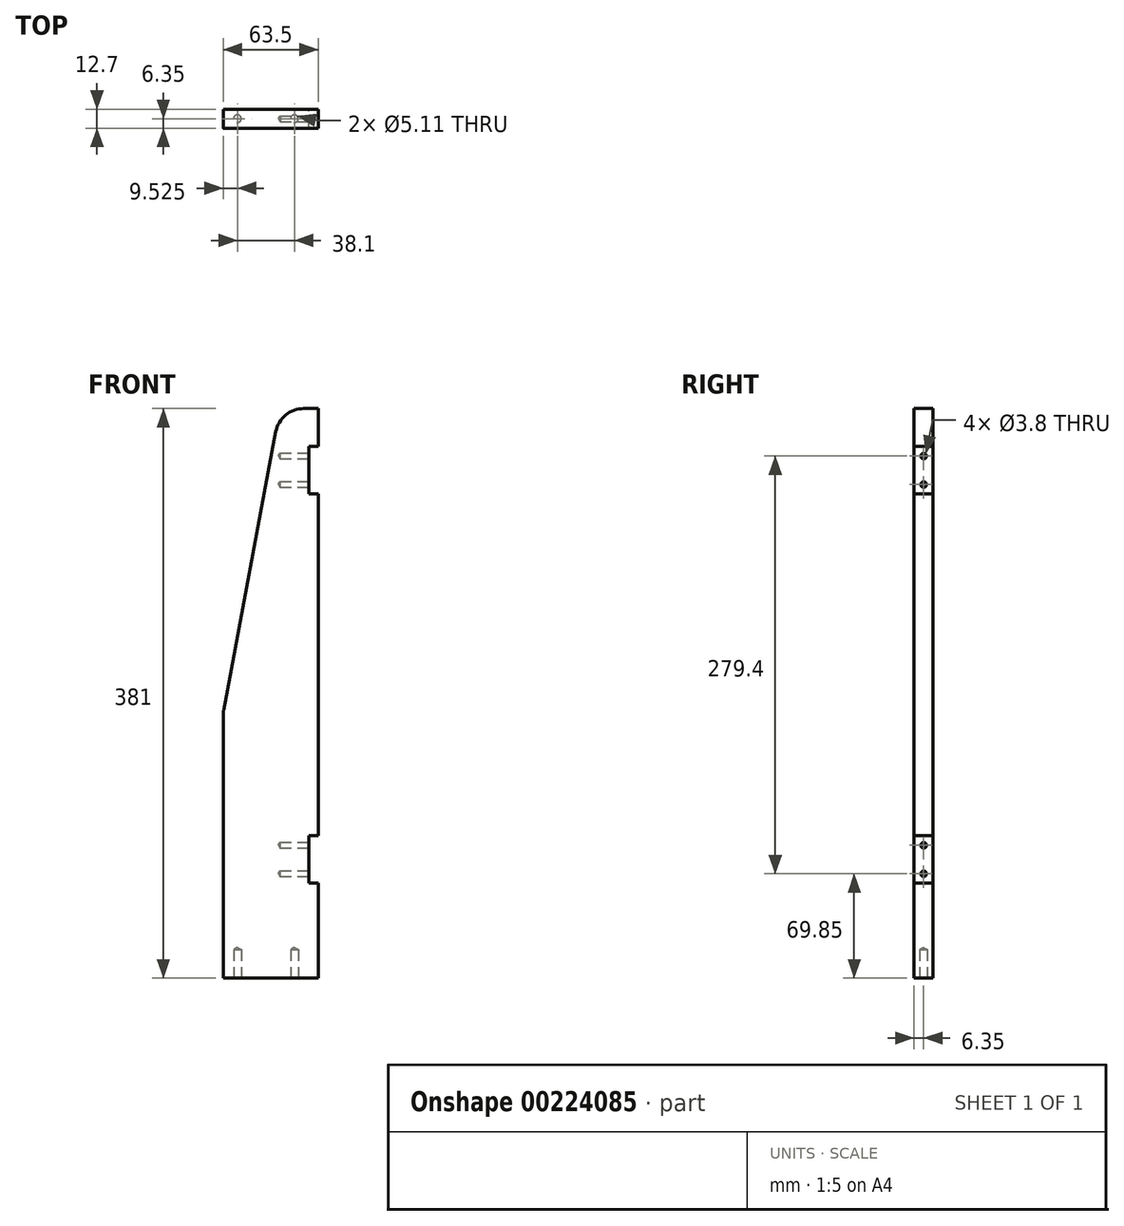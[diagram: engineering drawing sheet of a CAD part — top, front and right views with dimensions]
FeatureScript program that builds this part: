
annotation { "Feature Type Name" : "Feature", "Feature Type Description" : "" }
export const myFeature = defineFeature(function(context is Context, id is Id, definition is map)
    precondition{}
    {
        {
            var Q0;
            Q0=qCreatedBy(makeId("Top.planeOp"),FACE);
            var sketch = newSketch(context, id + "F0", { "sketchPlane" : qUnion([Q0])});
            skLineSegment(sketch, "E0.bottom", {"start": v(0, 0) * mm, "end": v(-63.5, 0) * mm});
            skLineSegment(sketch, "E0.top", {"start": v(0, 12.7) * mm, "end": v(-63.5, 12.7) * mm});
            skLineSegment(sketch, "E0.left", {"start": v(0, 0) * mm, "end": v(0, 12.7) * mm});
            skLineSegment(sketch, "E0.right", {"start": v(-63.5, 0) * mm, "end": v(-63.5, 12.7) * mm});
            skSolve(sketch);
        }
        {
            var Q0;
            Q0 = qSketchRegion(id + "F0", true);
            extrude(context, id + "F1", {"entities" : qUnion([Q0]), "depth" : 381 * mm});
        }
        {
            var Q0;
            Q0=makeQuery(id+"F1.opExtrude","CAP_FACE",FACE,{"disambiguationData":[OSD([sQuery(id+"F0.wireOp",EDGE,"E0.bottom"),sQuery(id+"F0.wireOp",EDGE,"E0.top"),sQuery(id+"F0.wireOp",EDGE,"E0.left"),sQuery(id+"F0.wireOp",EDGE,"E0.right")])],"isStart":true});
            var sketch = newSketch(context, id + "F2", { "sketchPlane" : qUnion([Q0])});
            skPoint(sketch, "E1", {"position": v(-15.88, -6.35) * mm});
            skPoint(sketch, "E2", {"position": v(-53.98, -6.35) * mm});
            skSolve(sketch);
        }
        {
            var Q0;
            Q0=sQuery(id+"F2.wireOp",VERTEX,"E1");
            var Q1;
            Q1=sQuery(id+"F2.wireOp",VERTEX,"E2");
            var Q2;
            Q2=makeQuery(id+"F1.opExtrude","SWEPT_BODY",BODY,{"disambiguationData":[OSD([sQuery(id+"F0.wireOp",EDGE,"E0.bottom"),sQuery(id+"F0.wireOp",EDGE,"E0.top"),sQuery(id+"F0.wireOp",EDGE,"E0.left"),sQuery(id+"F0.wireOp",EDGE,"E0.right")])]});
            hole(context, id + "F3", {"style" : HoleStyle.SIMPLE, "endStyle" : HoleEndStyle.BLIND, "standardTappedOrClearance" : lookupTablePath({ "standard" : "ANSI", "engagement" : "75%", "pitch" : "20 tpi", "size" : "1/4", "type" : "Tapped" }), "standardBlindInLast" : lookupTablePath({ "standard" : "ANSI", "engagement" : "75%", "pitch" : "20 tpi", "size" : "1/4", "type" : "Tapped" }), "holeDiameter" : 5.1 * mm, "holeDepth" : 19.05 * mm, "locations" : qUnion([Q0, Q1]), "scope" : qUnion([Q2]), "majorDiameter" : 6.35 * mm});
        }
        {
            var Q0;
            Q0=makeQuery(id+"F1.opExtrude","SWEPT_FACE",FACE,{"disambiguationData":[OSD([sQuery(id+"F0.wireOp",EDGE,"E0.left")])]});
            var sketch = newSketch(context, id + "F4", { "sketchPlane" : qUnion([Q0])});
            skLineSegment(sketch, "E3.bottom", {"start": v(0, 95.25) * mm, "end": v(50.8, 95.25) * mm});
            skLineSegment(sketch, "E3.top", {"start": v(0, 63.5) * mm, "end": v(50.8, 63.5) * mm});
            skLineSegment(sketch, "E3.left", {"start": v(0, 95.25) * mm, "end": v(0, 63.5) * mm});
            skLineSegment(sketch, "E3.right", {"start": v(50.8, 95.25) * mm, "end": v(50.8, 63.5) * mm});
            skLineSegment(sketch, "E4.bottom", {"start": v(0, 355.6) * mm, "end": v(50.8, 355.6) * mm});
            skLineSegment(sketch, "E4.top", {"start": v(0, 323.85) * mm, "end": v(50.8, 323.85) * mm});
            skLineSegment(sketch, "E4.left", {"start": v(0, 355.6) * mm, "end": v(0, 323.85) * mm});
            skLineSegment(sketch, "E4.right", {"start": v(50.8, 355.6) * mm, "end": v(50.8, 323.85) * mm});
            skSolve(sketch);
        }
        {
            var Q0;
            Q0 = qSketchRegion(id + "F4", true);
            extrude(context, id + "F5", {"entities" : qUnion([Q0]), "operationType" : NewBodyOperationType.REMOVE, "oppositeDirection" : true, "depth" : 6.35 * mm});
        }
        {
            var Q0;
            Q0=makeQuery(id+"F5.boolean.opBoolean","SPLIT",FACE,{"disambiguationData":[TD([makeQuery(id+"F5.opExtrude","SWEPT_FACE",FACE,{"disambiguationData":[OSD([sQuery(id+"F4.wireOp",EDGE,"E3.bottom")])]})])],"derivedFrom":makeQuery(id+"F1.opExtrude","SWEPT_FACE",FACE,{"disambiguationData":[OSD([sQuery(id+"F0.wireOp",EDGE,"E0.left")])]})});
            var sketch = newSketch(context, id + "F6", { "sketchPlane" : qUnion([Q0])});
            skPoint(sketch, "E5", {"position": v(6.35, 349.25) * mm});
            skPoint(sketch, "E6", {"position": v(6.35, 330.2) * mm});
            skPoint(sketch, "E7", {"position": v(6.35, 88.9) * mm});
            skPoint(sketch, "E8", {"position": v(6.35, 69.85) * mm});
            skSolve(sketch);
        }
        {
            var Q0;
            Q0=sQuery(id+"F6.wireOp",VERTEX,"E8");
            var Q1;
            Q1=sQuery(id+"F6.wireOp",VERTEX,"E7");
            var Q2;
            Q2=sQuery(id+"F6.wireOp",VERTEX,"E6");
            var Q3;
            Q3=sQuery(id+"F6.wireOp",VERTEX,"E5");
            var Q4;
            Q4=makeQuery(id+"F1.opExtrude","SWEPT_BODY",BODY,{"disambiguationData":[OSD([sQuery(id+"F0.wireOp",EDGE,"E0.bottom"),sQuery(id+"F0.wireOp",EDGE,"E0.top"),sQuery(id+"F0.wireOp",EDGE,"E0.left"),sQuery(id+"F0.wireOp",EDGE,"E0.right")])]});
            hole(context, id + "F7", {"style" : HoleStyle.SIMPLE, "endStyle" : HoleEndStyle.BLIND, "standardTappedOrClearance" : lookupTablePath({ "standard" : "ANSI", "engagement" : "75%", "pitch" : "24 tpi", "size" : "#10", "type" : "Tapped" }), "standardBlindInLast" : lookupTablePath({ "standard" : "ANSI", "engagement" : "75%", "pitch" : "24 tpi", "size" : "#10", "type" : "Tapped" }), "holeDiameter" : 3.8 * mm, "holeDepth" : 19.05 * mm, "locations" : qUnion([Q0, Q1, Q2, Q3]), "scope" : qUnion([Q4]), "majorDiameter" : 4.83 * mm});
        }
        {
            var Q0;
            Q0=makeQuery(id+"F1.opExtrude","CAP_EDGE",EDGE,{"disambiguationData":[OSD([sQuery(id+"F0.wireOp",EDGE,"E0.right")])],"isStart":false});
            chamfer(context, id + "F8", {"entities" : qUnion([Q0]), "chamferType" : ChamferType.TWO_OFFSETS, "width1" : 203.2 * mm, "oppositeDirection" : false, "width2" : 38.1 * mm, "tangentPropagation" : true});
        }
        {
            var Q0;
            {var subQ0=sQuery(id+"F0.wireOp",EDGE,"E0.right");Q0=makeQuery(id+"F8.opChamfer","BLEND_EDGE",EDGE,{"blendedFrom":[makeQuery(id+"F1.opExtrude","CAP_EDGE",EDGE,{"disambiguationData":[OSD([subQ0])],"isStart":false}),makeQuery(id+"F1.opExtrude","CAP_FACE",FACE,{"disambiguationData":[OSD([sQuery(id+"F0.wireOp",EDGE,"E0.bottom"),sQuery(id+"F0.wireOp",EDGE,"E0.top"),sQuery(id+"F0.wireOp",EDGE,"E0.left"),subQ0])],"isStart":false})],"blendedInto":[makeQuery(id+"F1.opExtrude","CAP_FACE",FACE,{"disambiguationData":[OSD([sQuery(id+"F0.wireOp",EDGE,"E0.bottom"),sQuery(id+"F0.wireOp",EDGE,"E0.top"),sQuery(id+"F0.wireOp",EDGE,"E0.left"),subQ0])],"isStart":false})]});}
            var Q1;
            {var subQ0=sQuery(id+"F0.wireOp",EDGE,"E0.right");Q1=makeQuery(id+"F8.opChamfer","BLEND_EDGE",EDGE,{"blendedFrom":[makeQuery(id+"F1.opExtrude","CAP_EDGE",EDGE,{"disambiguationData":[OSD([subQ0])],"isStart":false}),makeQuery(id+"F1.opExtrude","SWEPT_FACE",FACE,{"disambiguationData":[OSD([subQ0])]})],"blendedInto":[makeQuery(id+"F1.opExtrude","SWEPT_FACE",FACE,{"disambiguationData":[OSD([subQ0])]})]});}
            fillet(context, id + "F9", {"entities" : qUnion([Q0, Q1]), "radius" : 19.05 * mm, "tangentPropagation" : true, "allowEdgeOverflow" : false});
        }
    });
